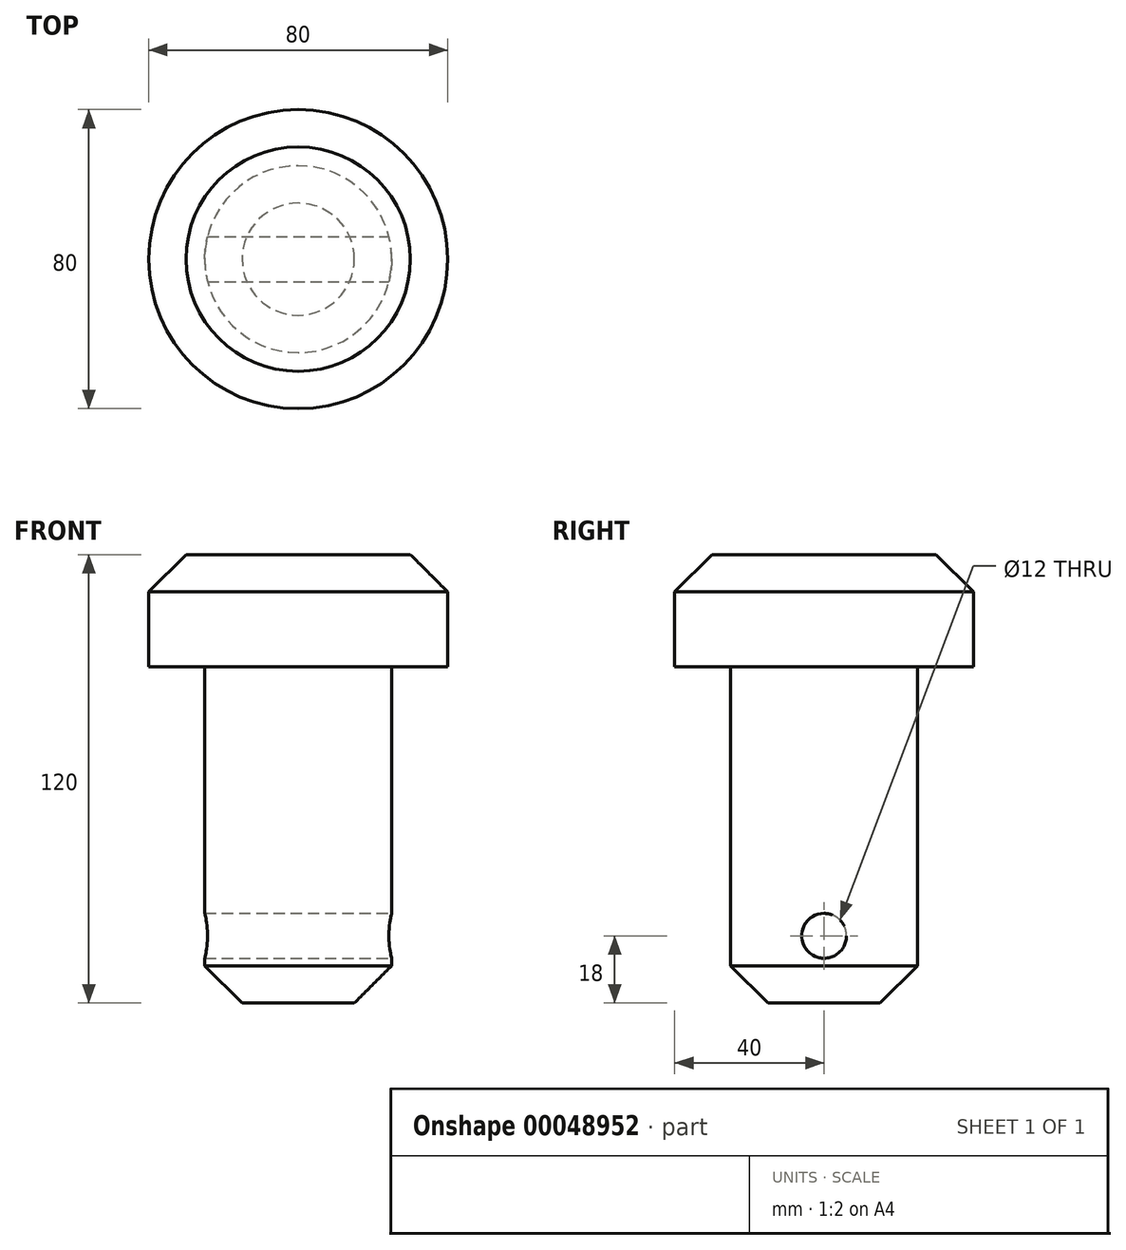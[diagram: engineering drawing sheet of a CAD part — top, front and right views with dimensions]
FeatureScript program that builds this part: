
annotation { "Feature Type Name" : "Feature", "Feature Type Description" : "" }
export const myFeature = defineFeature(function(context is Context, id is Id, definition is map)
    precondition{}
    {
        {
            var Q0;
            Q0=qCreatedBy(makeId("Top.planeOp"),FACE);
            var sketch = newSketch(context, id + "F0", { "sketchPlane" : qUnion([Q0])});
            skCircle(sketch, "E0", {"center": v(0, 0) * mm, "radius": 25 * mm});
            skSolve(sketch);
        }
        {
            var Q0;
            Q0=makeQuery(id+"F0.imprint","IMPRINT",FACE,{"disambiguationData":[TD([[makeQuery(id+"F0.imprint","IMPRINT",EDGE,{"derivedFrom":sQuery(id+"F0.wireOp",EDGE,"E0")}),1.0]])]});
            extrude(context, id + "F1", {"entities" : qUnion([Q0]), "depth" : 90 * mm});
        }
        {
            var Q0;
            Q0=makeQuery(id+"F1.opExtrude","CAP_FACE",FACE,{"disambiguationData":[OSD([sQuery(id+"F0.wireOp",EDGE,"E0")])],"isStart":false});
            var sketch = newSketch(context, id + "F2", { "sketchPlane" : qUnion([Q0])});
            skCircle(sketch, "E1", {"center": v(0, 0) * mm, "radius": 40 * mm});
            skSolve(sketch);
        }
        {
            var Q0;
            Q0=makeQuery(id+"F2.imprint","IMPRINT",FACE,{"disambiguationData":[TD([[makeQuery(id+"F2.imprint","IMPRINT",EDGE,{"derivedFrom":makeQuery(id+"F1.opExtrude","CAP_EDGE",EDGE,{"disambiguationData":[OSD([sQuery(id+"F0.wireOp",EDGE,"E0")])],"isStart":false})}),1.0]])]});
            var Q1;
            Q1=makeQuery(id+"F2.imprint","IMPRINT",FACE,{"disambiguationData":[TD([[makeQuery(id+"F2.imprint","IMPRINT",EDGE,{"derivedFrom":sQuery(id+"F2.wireOp",EDGE,"E1")}),1.0]])]});
            extrude(context, id + "F3", {"entities" : qUnion([Q0, Q1]), "operationType" : NewBodyOperationType.ADD, "depth" : 30 * mm});
        }
        {
            var Q0;
            Q0=makeQuery(id+"F3.opExtrude","CAP_EDGE",EDGE,{"disambiguationData":[OSD([sQuery(id+"F2.wireOp",EDGE,"E1")])],"isStart":false});
            chamfer(context, id + "F4", {"entities" : qUnion([Q0]), "chamferType" : ChamferType.OFFSET_ANGLE, "width" : 10 * mm, "oppositeDirection" : false, "angle" : 45 * degree, "tangentPropagation" : true});
        }
        {
            var Q0;
            Q0=qCreatedBy(makeId("Right.planeOp"),FACE);
            cPlane(context, id + "F5", {"entities" : qUnion([Q0]), "cplaneType" : CPlaneType.OFFSET, "offset" : 25 * mm, "width" : 150 * mm, "height" : 150 * mm});
        }
        {
            var Q0;
            Q0=qCreatedBy(id+"F5.planeOp",FACE);
            var sketch = newSketch(context, id + "F6", { "sketchPlane" : qUnion([Q0])});
            skLineSegment(sketch, "E2", {"start": v(0, 0) * mm, "end": v(0, 18) * mm, "construction": true});
            skCircle(sketch, "E3", {"center": v(0, 18) * mm, "radius": 6 * mm});
            skSolve(sketch);
        }
        {
            var Q0;
            Q0=makeQuery(id+"F6.imprint","IMPRINT",FACE,{"disambiguationData":[TD([[makeQuery(id+"F6.imprint","IMPRINT",EDGE,{"derivedFrom":sQuery(id+"F6.wireOp",EDGE,"E3")}),1.0]])]});
            extrude(context, id + "F7", {"entities" : qUnion([Q0]), "operationType" : NewBodyOperationType.REMOVE, "endBound" : BoundingType.THROUGH_ALL, "oppositeDirection" : true, "depth" : 25 * mm});
        }
        {
            var Q0;
            Q0=makeQuery(id+"F1.opExtrude","CAP_EDGE",EDGE,{"disambiguationData":[OSD([sQuery(id+"F0.wireOp",EDGE,"E0")])],"isStart":true});
            chamfer(context, id + "F8", {"entities" : qUnion([Q0]), "chamferType" : ChamferType.OFFSET_ANGLE, "width" : 10 * mm, "oppositeDirection" : false, "angle" : 45 * degree, "tangentPropagation" : true});
        }
    });
